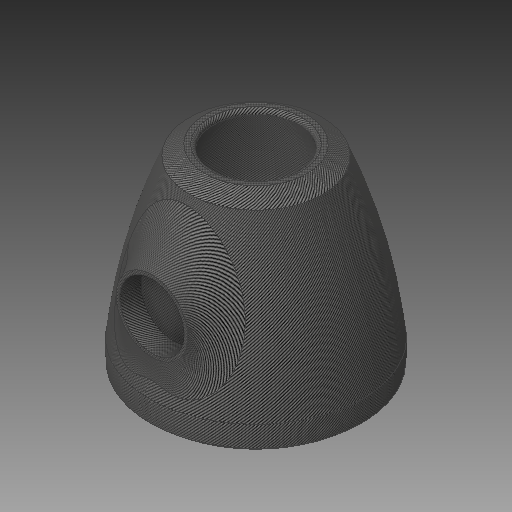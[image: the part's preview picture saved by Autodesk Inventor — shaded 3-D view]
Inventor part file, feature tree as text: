
AUTODESK INVENTOR PART (.ipt)
format: ipt  version: 2018 (Build 220112000, 112)  size: 410,112 bytes
history: native  units: in
note: dims shown in document units (in); Inventor stores cm internally (conversion verified against a paired STEP export)
features: sketch x4, other x3
ambient origin geometry x8: Origin, YZ Plane, XZ Plane, XY Plane, X Axis, Y Axis, Z Axis, Center Point
bodies: Solid1 (feature_tree)
feature tree (7):
  other  "arm_cup 5,6.ipt"
  other  "Solid1::arm_cup 5,6.ipt"
  other  "TaggingFeature1"
  sketch  "Sketch1"  dims[d0=0.3937in]
  sketch  "Sketch2"
  sketch  "Sketch3"
  sketch  "Sketch4"
